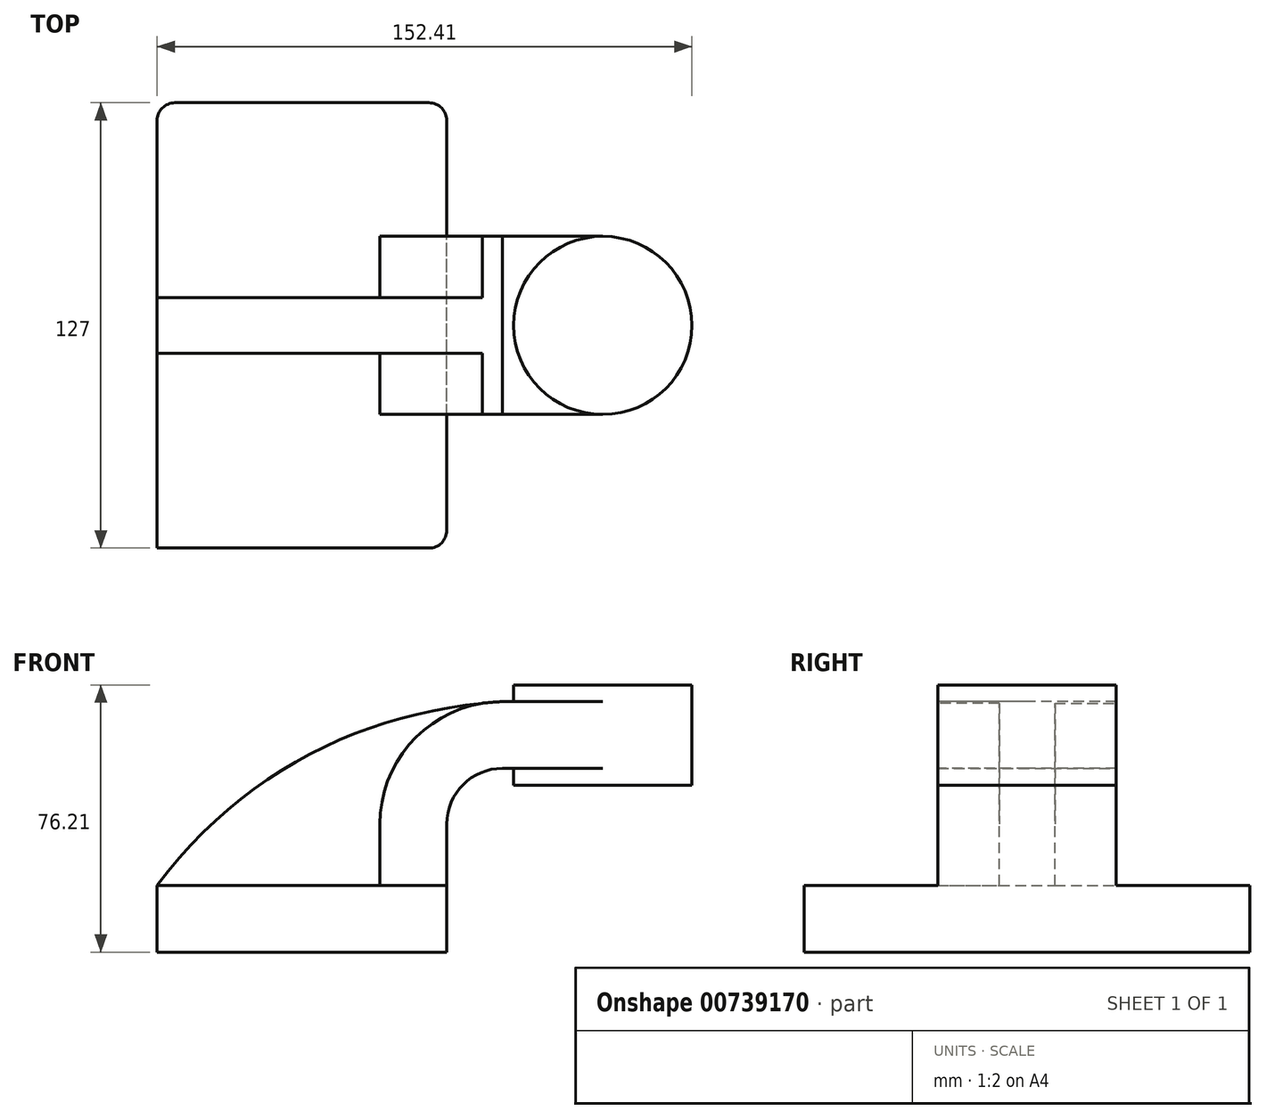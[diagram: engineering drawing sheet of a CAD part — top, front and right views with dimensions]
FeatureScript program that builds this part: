
annotation { "Feature Type Name" : "Feature", "Feature Type Description" : "" }
export const myFeature = defineFeature(function(context is Context, id is Id, definition is map)
    precondition{}
    {
        {
            var Q0;
            Q0=qCreatedBy(makeId("Front.planeOp"),FACE);
            var sketch = newSketch(context, id + "F0", { "sketchPlane" : qUnion([Q0])});
            skLineSegment(sketch, "E0.bottom", {"start": v(41.27, 9.53) * mm, "end": v(-41.27, 9.53) * mm});
            skLineSegment(sketch, "E0.top", {"start": v(41.28, -9.52) * mm, "end": v(-41.27, -9.52) * mm});
            skLineSegment(sketch, "E0.left", {"start": v(41.28, 9.53) * mm, "end": v(41.28, -9.52) * mm});
            skLineSegment(sketch, "E0.right", {"start": v(-41.27, 9.53) * mm, "end": v(-41.27, -9.52) * mm});
            skPoint(sketch, "E0.middle", {"position": v(0, 0) * mm});
            skLineSegment(sketch, "E1.bottom", {"start": v(111.13, 66.68) * mm, "end": v(60.32, 66.68) * mm});
            skLineSegment(sketch, "E1.top", {"start": v(111.13, 38.1) * mm, "end": v(60.32, 38.1) * mm});
            skLineSegment(sketch, "E1.left", {"start": v(111.13, 66.68) * mm, "end": v(111.13, 38.1) * mm});
            skLineSegment(sketch, "E1.right", {"start": v(60.32, 66.68) * mm, "end": v(60.32, 38.1) * mm});
            skPoint(sketch, "E1.middle", {"position": v(85.72, 52.39) * mm});
            skLineSegment(sketch, "E2", {"start": v(41.27, 9.53) * mm, "end": v(41.27, 27) * mm});
            skArc(sketch, "E3", {"start": v(41.27, 27) * mm, "mid": v(45.92, 38.23) * mm, "end": v(57.15, 42.88) * mm});
            skLineSegment(sketch, "E4", {"start": v(57.15, 42.88) * mm, "end": v(85.72, 42.88) * mm});
            skLineSegment(sketch, "E5.0", {"start": v(57.15, 61.93) * mm, "end": v(85.73, 61.93) * mm});
            skArc(sketch, "E5.1", {"start": v(22.22, 27) * mm, "mid": v(32.45, 51.7) * mm, "end": v(57.15, 61.93) * mm});
            skLineSegment(sketch, "E5.2", {"start": v(22.22, 9.53) * mm, "end": v(22.22, 27) * mm});
            skLineSegment(sketch, "E6", {"start": v(85.72, 38.1) * mm, "end": v(85.72, 66.68) * mm});
            skFitSpline(sketch, "E7", {"points": [v(-41.28, 9.53) * mm, v(57.15, 61.93) * mm], "startDerivative": vector(73.9, 99) * mm, "endDerivative": vector(115.6, 7.44) * mm});
            skSolve(sketch);
        }
        {
            var Q0;
            Q0=makeQuery(id+"F0.imprint","IMPRINT",FACE,{"disambiguationData":[TD([[makeQuery(id+"F0.imprint","IMPRINT",EDGE,{"derivedFrom":sQuery(id+"F0.wireOp",EDGE,"E0.top")}),-1.0]])]});
            extrude(context, id + "F1", {"entities" : qUnion([Q0]), "endBound" : BoundingType.SYMMETRIC, "depth" : 127 * mm, "offsetDistance" : 25.4 * mm});
        }
        {
            var Q0;
            {var subQ1=sQuery(id+"F0.wireOp",EDGE,"E2");Q0=makeQuery(id+"F0.imprint","IMPRINT",FACE,{"disambiguationData":[TD([[makeQuery(id+"F0.imprint","IMPRINT",EDGE,{"derivedFrom":subQ1}),1.0]])]});}
            extrude(context, id + "F2", {"entities" : qUnion([Q0]), "operationType" : NewBodyOperationType.ADD, "endBound" : BoundingType.SYMMETRIC, "depth" : 50.8 * mm, "offsetDistance" : 25.4 * mm});
        }
        {
            var Q0;
            {var subQ0=sQuery(id+"F0.wireOp",EDGE,"E5.0");var subQ1=sQuery(id+"F0.wireOp",EDGE,"E1.right");var subQ2=makeQuery(id+"F0.imprint","INTERSECT",VERTEX,{"derivedFrom":[subQ1,subQ0]});Q0=makeQuery(id+"F0.imprint","IMPRINT",FACE,{"disambiguationData":[TD([[makeQuery(id+"F0.imprint","IMPRINT",EDGE,{"disambiguationData":[TD([[subQ2,-1.0]])],"derivedFrom":subQ1}),1.0]])]});}
            extrude(context, id + "F3", {"entities" : qUnion([Q0]), "operationType" : NewBodyOperationType.ADD, "endBound" : BoundingType.SYMMETRIC, "depth" : 50.8 * mm, "offsetDistance" : 25.4 * mm});
        }
        {
            var Q0;
            {var subQ3=sQuery(id+"F0.wireOp",EDGE,"E5.2");Q0=makeQuery(id+"F0.imprint","IMPRINT",FACE,{"disambiguationData":[TD([[makeQuery(id+"F0.imprint","IMPRINT",EDGE,{"derivedFrom":subQ3}),1.0]])]});}
            extrude(context, id + "F4", {"entities" : qUnion([Q0]), "operationType" : NewBodyOperationType.ADD, "endBound" : BoundingType.SYMMETRIC, "depth" : 15.88 * mm, "offsetDistance" : 25.4 * mm});
        }
        {
            var Q0;
            {var subQ0=sQuery(id+"F0.wireOp",EDGE,"E1.left");Q0=makeQuery(id+"F0.imprint","IMPRINT",FACE,{"disambiguationData":[TD([[makeQuery(id+"F0.imprint","IMPRINT",EDGE,{"derivedFrom":subQ0}),-1.0]])]});}
            var Q1;
            Q1=sQuery(id+"F0.wireOp",EDGE,"E6");
            revolve(context, id + "F5", {"operationType" : NewBodyOperationType.ADD, "surfaceOperationType" : NewSurfaceOperationType.NEW, "entities" : qUnion([Q0]), "axis" : qUnion([Q1]), "revolveType" : RevolveType.FULL});
        }
        {
            var Q0;
            Q0=makeQuery(id+"F1.opExtrude","CAP_EDGE",EDGE,{"disambiguationData":[OSD([sQuery(id+"F0.wireOp",EDGE,"E0.left")])],"isStart":false});
            var Q1;
            Q1=makeQuery(id+"F1.opExtrude","CAP_EDGE",EDGE,{"disambiguationData":[OSD([sQuery(id+"F0.wireOp",EDGE,"E0.right")])],"isStart":true});
            var Q2;
            Q2=makeQuery(id+"F1.opExtrude","CAP_EDGE",EDGE,{"disambiguationData":[OSD([sQuery(id+"F0.wireOp",EDGE,"E0.left")])],"isStart":true});
            fillet(context, id + "F6", {"entities" : qUnion([Q0, Q1, Q2]), "radius" : 5.08 * mm, "tangentPropagation" : true, "allowEdgeOverflow" : false});
        }
    });
